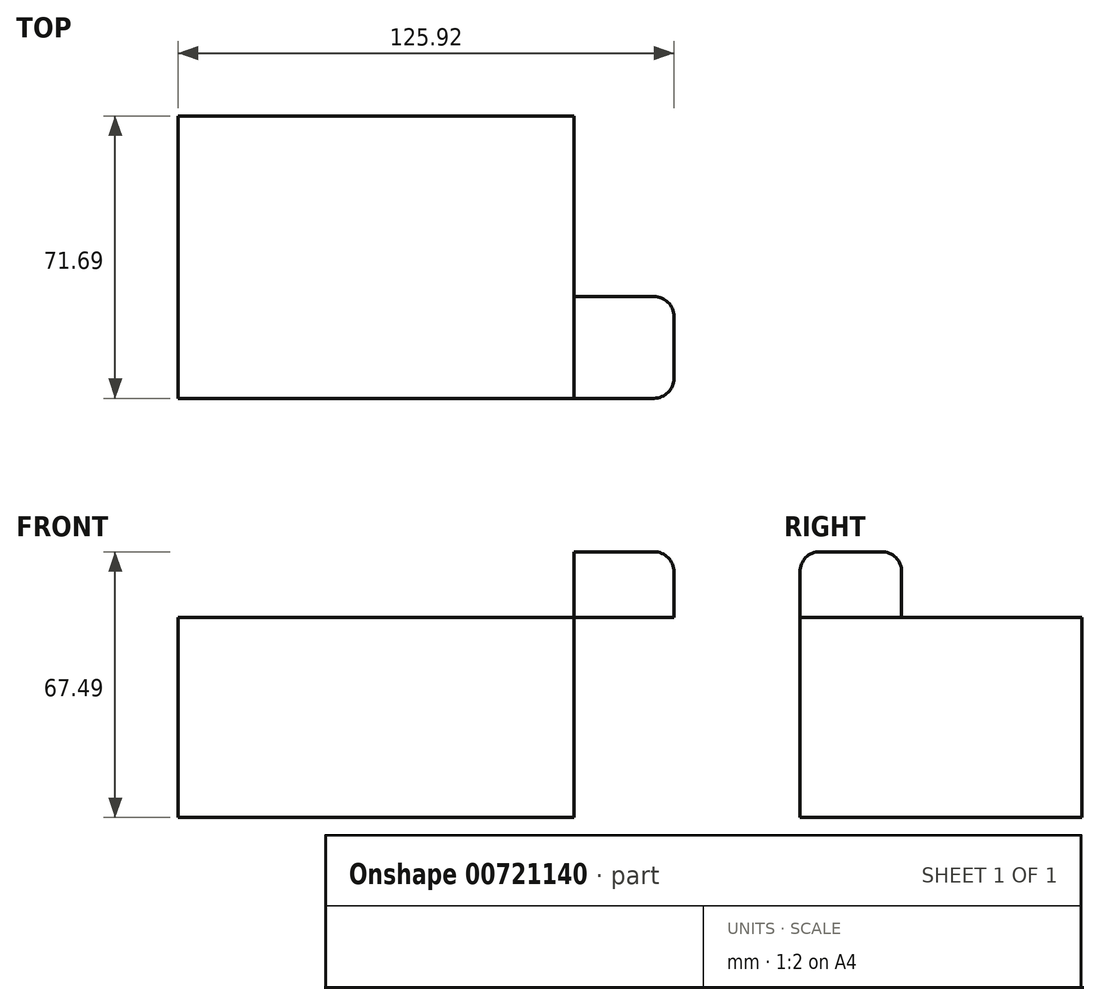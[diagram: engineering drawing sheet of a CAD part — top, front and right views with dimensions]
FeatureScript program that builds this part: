
annotation { "Feature Type Name" : "Feature", "Feature Type Description" : "" }
export const myFeature = defineFeature(function(context is Context, id is Id, definition is map)
    precondition{}
    {
        {
            var Q0;
            Q0=qCreatedBy(makeId("Top.planeOp"),FACE);
            var sketch = newSketch(context, id + "F0", { "sketchPlane" : qUnion([Q0])});
            skLineSegment(sketch, "E0.bottom", {"start": v(43.24, 45.82) * mm, "end": v(-57.28, 45.82) * mm});
            skLineSegment(sketch, "E0.top", {"start": v(43.24, -25.87) * mm, "end": v(-57.28, -25.87) * mm});
            skLineSegment(sketch, "E0.left", {"start": v(43.24, 45.82) * mm, "end": v(43.24, -25.87) * mm});
            skLineSegment(sketch, "E0.right", {"start": v(-57.28, 45.82) * mm, "end": v(-57.28, -25.87) * mm});
            skSolve(sketch);
        }
        {
            var Q0;
            Q0=makeQuery(id+"F0.imprint","IMPRINT",FACE,{"disambiguationData":[TD([[makeQuery(id+"F0.imprint","IMPRINT",EDGE,{"derivedFrom":sQuery(id+"F0.wireOp",EDGE,"E0.bottom")}),1.0]])]});
            extrude(context, id + "F1", {"entities" : qUnion([Q0]), "depth" : 50.8 * mm, "offsetDistance" : 25.4 * mm});
        }
        {
            var Q0;
            Q0=makeQuery(id+"F1.opExtrude","SWEPT_FACE",FACE,{"disambiguationData":[OSD([sQuery(id+"F0.wireOp",EDGE,"E0.left")])]});
            var sketch = newSketch(context, id + "F2", { "sketchPlane" : qUnion([Q0])});
            skLineSegment(sketch, "E1.bottom", {"start": v(0, 67.49) * mm, "end": v(-25.87, 67.49) * mm});
            skLineSegment(sketch, "E1.top", {"start": v(0, 50.8) * mm, "end": v(-25.87, 50.8) * mm});
            skLineSegment(sketch, "E1.left", {"start": v(0, 67.49) * mm, "end": v(0, 50.8) * mm});
            skLineSegment(sketch, "E1.right", {"start": v(-25.87, 67.49) * mm, "end": v(-25.87, 50.8) * mm});
            skSolve(sketch);
        }
        {
            var Q0;
            Q0 = qSketchRegion(id + "F2", true);
            extrude(context, id + "F3", {"entities" : qUnion([Q0]), "depth" : 25.4 * mm, "offsetDistance" : 25.4 * mm});
        }
        {
            var Q0;
            Q0=makeQuery(id+"F3.opExtrude","SWEPT_EDGE",EDGE,{"disambiguationData":[OSD([sQuery(id+"F2.wireOp",EDGE,"E1.bottom"),sQuery(id+"F2.wireOp",EDGE,"E1.left")])]});
            fillet(context, id + "F4", {"entities" : qUnion([Q0]), "radius" : 5.08 * mm, "tangentPropagation" : true, "allowEdgeOverflow" : false});
        }
        {
            var Q0;
            Q0=makeQuery(id+"F3.opExtrude","SWEPT_EDGE",EDGE,{"disambiguationData":[OSD([sQuery(id+"F2.wireOp",EDGE,"E1.bottom"),sQuery(id+"F2.wireOp",EDGE,"E1.right")])]});
            fillet(context, id + "F5", {"entities" : qUnion([Q0]), "radius" : 5.08 * mm, "tangentPropagation" : true, "allowEdgeOverflow" : false});
        }
        {
            var Q0;
            Q0=makeQuery(id+"F3.opExtrude","CAP_EDGE",EDGE,{"disambiguationData":[OSD([sQuery(id+"F2.wireOp",EDGE,"E1.bottom")])],"isStart":false});
            fillet(context, id + "F6", {"entities" : qUnion([Q0]), "radius" : 5.08 * mm, "tangentPropagation" : true, "allowEdgeOverflow" : false});
        }
    });
